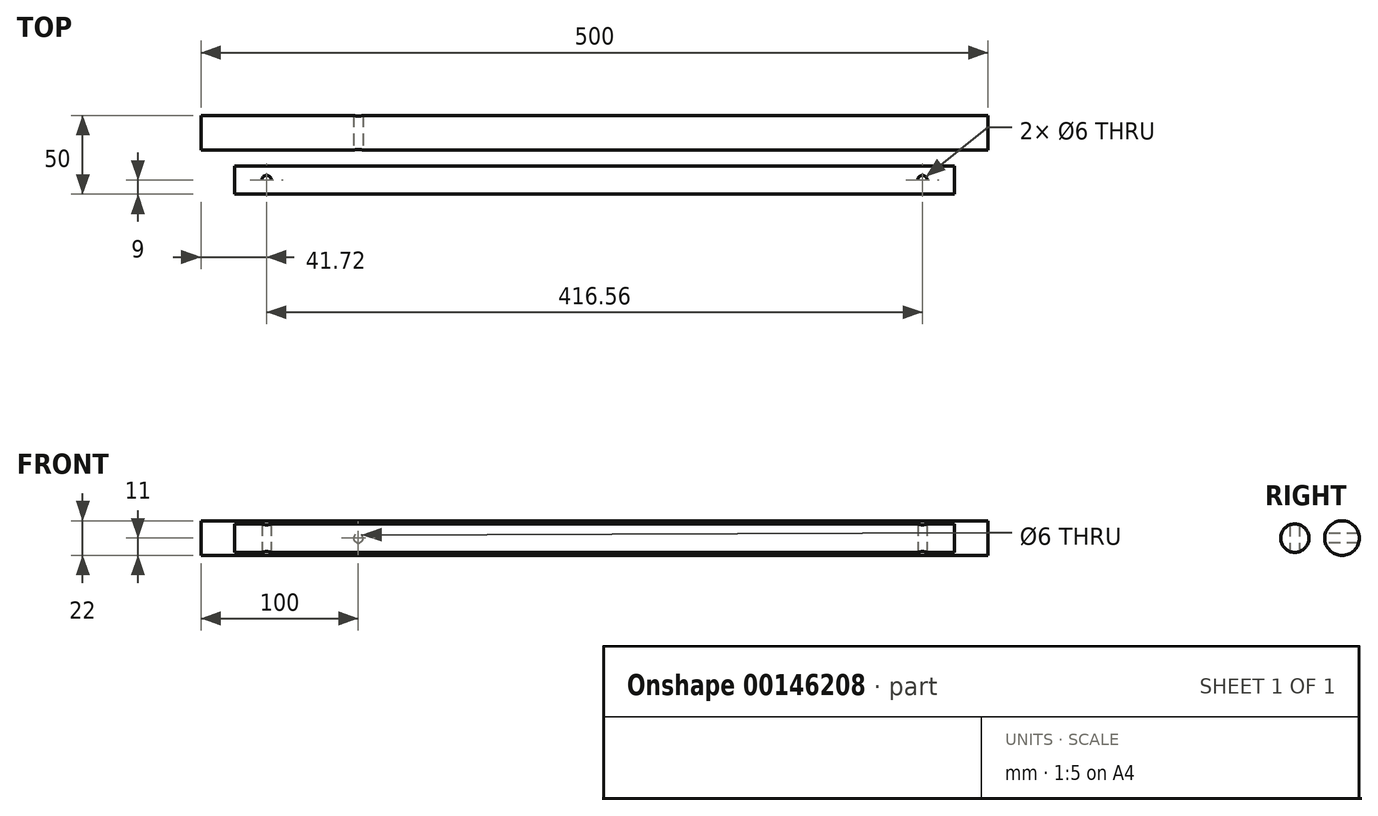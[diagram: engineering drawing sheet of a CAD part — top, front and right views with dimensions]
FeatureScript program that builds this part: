
annotation { "Feature Type Name" : "Feature", "Feature Type Description" : "" }
export const myFeature = defineFeature(function(context is Context, id is Id, definition is map)
    precondition{}
    {
        {
            var Q0;
            Q0=qCreatedBy(makeId("Right.planeOp"),FACE);
            var sketch = newSketch(context, id + "F0", { "sketchPlane" : qUnion([Q0])});
            skCircle(sketch, "E0", {"center": v(0, 0) * mm, "radius": 11 * mm});
            skCircle(sketch, "E1", {"center": v(-30, 0) * mm, "radius": 9 * mm});
            skSolve(sketch);
        }
        {
            var Q0;
            Q0=makeQuery(id+"F0.imprint","IMPRINT",FACE,{"disambiguationData":[TD([[makeQuery(id+"F0.imprint","IMPRINT",EDGE,{"derivedFrom":sQuery(id+"F0.wireOp",EDGE,"E0")}),1.0]])]});
            extrude(context, id + "F1", {"entities" : qUnion([Q0]), "depth" : 500 * mm, "symmetric" : true});
        }
        {
            var Q0;
            Q0=qCreatedBy(makeId("Front.planeOp"),FACE);
            var sketch = newSketch(context, id + "F2", { "sketchPlane" : qUnion([Q0])});
            skCircle(sketch, "E2", {"center": v(-150, 0) * mm, "radius": 3 * mm});
            skSolve(sketch);
        }
        {
            var Q0;
            Q0 = qSketchRegion(id + "F2", true);
            var Q1;
            Q1=sQuery(id+"F2.wireOp",EDGE,"E2");
            extrude(context, id + "F3", {"entities" : qUnion([Q0]), "operationType" : NewBodyOperationType.REMOVE, "surfaceEntities" : qUnion([Q1]), "oppositeDirection" : true, "depth" : 25.4 * mm, "symmetric" : true});
        }
        {
            var Q0;
            Q0=makeQuery(id+"F0.imprint","IMPRINT",FACE,{"disambiguationData":[TD([[makeQuery(id+"F0.imprint","IMPRINT",EDGE,{"derivedFrom":sQuery(id+"F0.wireOp",EDGE,"E1")}),1.0]])]});
            var Q1;
            Q1=sQuery(id+"F0.wireOp",EDGE,"E1");
            extrude(context, id + "F4", {"entities" : qUnion([Q0]), "operationType" : NewBodyOperationType.ADD, "surfaceEntities" : qUnion([Q1]), "depth" : 457.2 * mm, "symmetric" : true});
        }
        {
            var Q0;
            Q0=qCreatedBy(makeId("Top.planeOp"),FACE);
            var sketch = newSketch(context, id + "F5", { "sketchPlane" : qUnion([Q0])});
            skLineSegment(sketch, "E3", {"start": v(0, 0) * mm, "end": v(0, -30) * mm});
            skCircle(sketch, "E4", {"center": v(-208.28, -30) * mm, "radius": 3 * mm});
            skLineSegment(sketch, "E5", {"start": v(-208.28, -30) * mm, "end": v(0, -30) * mm});
            skCircle(sketch, "E6.MirrorC", {"center": v(208.28, -30) * mm, "radius": 3 * mm});
            skSolve(sketch);
        }
        {
            var Q0;
            Q0 = qSketchRegion(id + "F5", true);
            var Q1;
            Q1=sQuery(id+"F5.wireOp",EDGE,"E4");
            var Q2;
            Q2=sQuery(id+"F5.wireOp",EDGE,"E6.MirrorC");
            extrude(context, id + "F6", {"entities" : qUnion([Q0]), "operationType" : NewBodyOperationType.REMOVE, "surfaceEntities" : qUnion([Q1, Q2]), "depth" : 25.4 * mm, "symmetric" : true});
        }
    });
